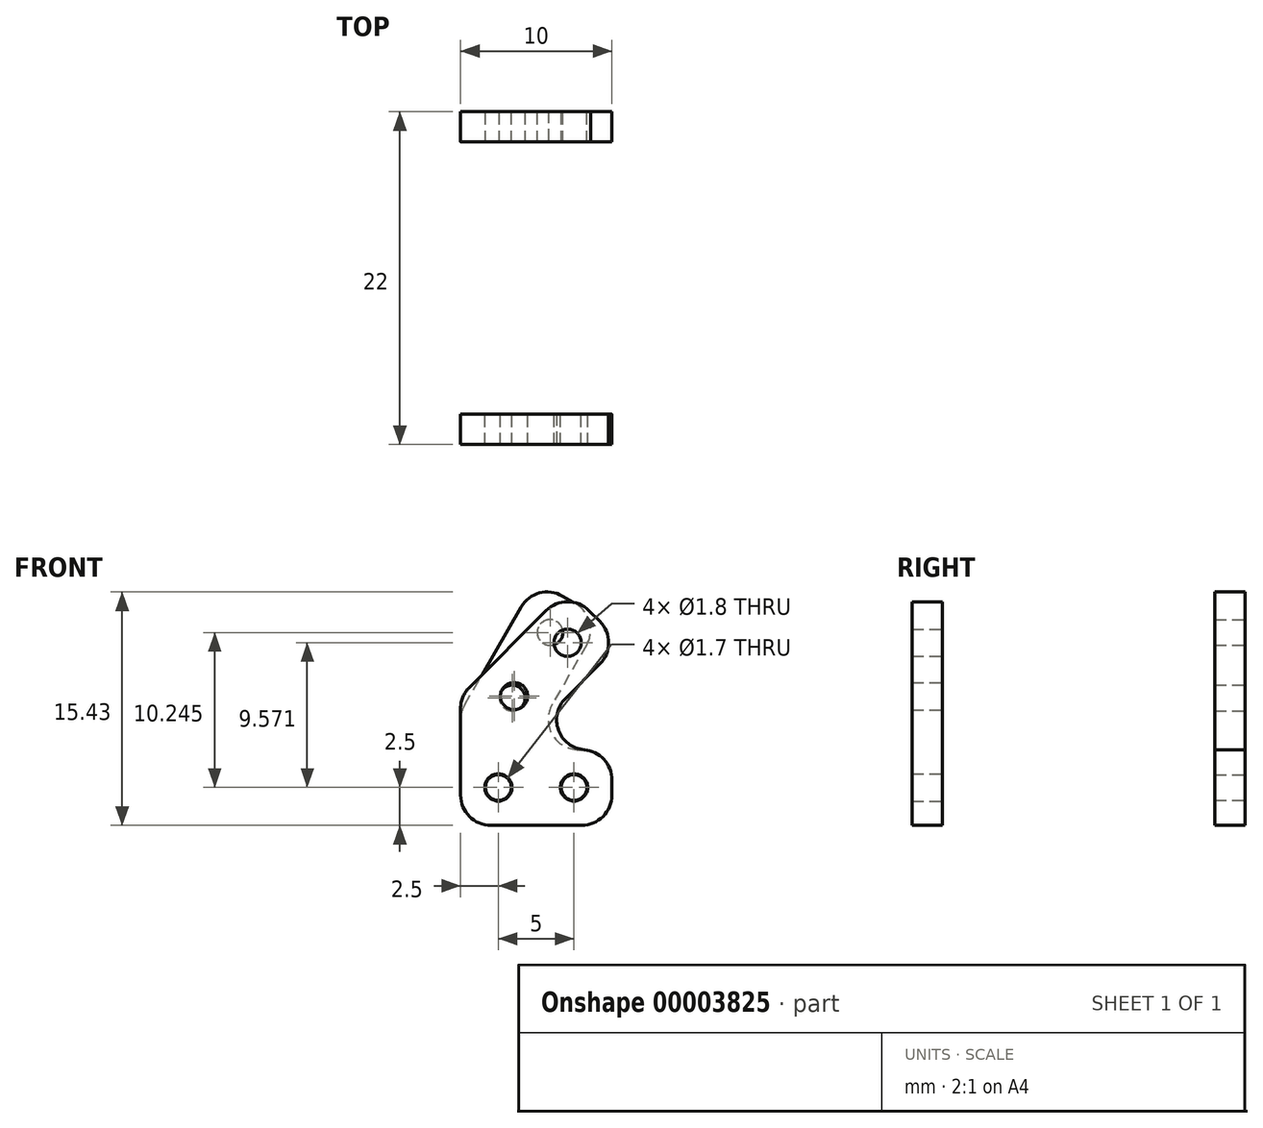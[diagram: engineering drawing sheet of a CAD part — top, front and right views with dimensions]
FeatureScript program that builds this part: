
annotation { "Feature Type Name" : "Feature", "Feature Type Description" : "" }
export const myFeature = defineFeature(function(context is Context, id is Id, definition is map)
    precondition{}
    {
        {
            var Q0;
            Q0=qCreatedBy(makeId("Front.planeOp"),FACE);
            var sketch = newSketch(context, id + "F0", { "sketchPlane" : qUnion([Q0])});
            skLineSegment(sketch, "E0", {"start": v(0, 0) * mm, "end": v(0, 7.5) * mm});
            skLineSegment(sketch, "E1", {"start": v(0, 7.5) * mm, "end": v(5, 16.16) * mm});
            skLineSegment(sketch, "E2", {"start": v(5, 16.16) * mm, "end": v(9.33, 13.66) * mm});
            skLineSegment(sketch, "E3", {"start": v(9.33, 13.66) * mm, "end": v(4.33, 5) * mm});
            skLineSegment(sketch, "E4", {"start": v(4.33, 5) * mm, "end": v(10, 5) * mm});
            skLineSegment(sketch, "E5", {"start": v(10, 5) * mm, "end": v(10, 0) * mm});
            skLineSegment(sketch, "E6", {"start": v(10, 0) * mm, "end": v(0, 0) * mm});
            skLineSegment(sketch, "E7", {"start": v(7.17, 14.91) * mm, "end": v(2.15, 6.22) * mm, "construction": true});
            skCircle(sketch, "E8", {"center": v(5.92, 12.75) * mm, "radius": 0.85 * mm});
            skCircle(sketch, "E9", {"center": v(3.42, 8.42) * mm, "radius": 0.85 * mm});
            skLineSegment(sketch, "E10", {"start": v(10, 2.5) * mm, "end": v(0, 2.5) * mm, "construction": true});
            skCircle(sketch, "E11", {"center": v(2.5, 2.5) * mm, "radius": 0.85 * mm});
            skCircle(sketch, "E12", {"center": v(7.5, 2.5) * mm, "radius": 0.85 * mm});
            skPoint(sketch, "E13.visualSharp", {"position": v(0, 0) * mm});
            skPoint(sketch, "E14.visualSharp", {"position": v(10, 0) * mm});
            skPoint(sketch, "E15.visualSharp", {"position": v(10, 5) * mm});
            skPoint(sketch, "E16.visualSharp", {"position": v(4.33, 5) * mm});
            skPoint(sketch, "E17.visualSharp", {"position": v(9.33, 13.66) * mm});
            skPoint(sketch, "E18.visualSharp", {"position": v(5, 16.16) * mm});
            skPoint(sketch, "E19.visualSharp", {"position": v(0, 7.5) * mm});
            skSolve(sketch);
        }
        {
            var Q0;
            Q0=makeQuery(id+"F0.imprint","IMPRINT",FACE,{"disambiguationData":[TD([[makeQuery(id+"F0.imprint","IMPRINT",EDGE,{"derivedFrom":sQuery(id+"F0.wireOp",EDGE,"E0")}),-1.0]])]});
            extrude(context, id + "F1", {"entities" : qUnion([Q0]), "depth" : 2 * mm});
        }
        {
            var Q0;
            Q0=qCreatedBy(makeId("Front.planeOp"),FACE);
            cPlane(context, id + "F2", {"entities" : qUnion([Q0]), "cplaneType" : CPlaneType.OFFSET, "offset" : 20 * mm, "width" : 150 * mm, "height" : 150 * mm});
        }
        {
            var Q0;
            Q0=qCreatedBy(id+"F2.planeOp",FACE);
            var sketch = newSketch(context, id + "F3", { "sketchPlane" : qUnion([Q0])});
            skLineSegment(sketch, "E20.bottom", {"start": v(0, 0) * mm, "end": v(10, 0) * mm});
            skLineSegment(sketch, "E20.left", {"start": v(0, 0) * mm, "end": v(0, 8.54) * mm});
            skLineSegment(sketch, "E20.right", {"start": v(10, 0) * mm, "end": v(10, 5) * mm});
            skLineSegment(sketch, "E21", {"start": v(0, 8.54) * mm, "end": v(7.07, 15.6) * mm});
            skLineSegment(sketch, "E22", {"start": v(7.07, 15.6) * mm, "end": v(10.6, 12.07) * mm});
            skLineSegment(sketch, "E23", {"start": v(10.6, 12.07) * mm, "end": v(3.54, 5) * mm});
            skLineSegment(sketch, "E24", {"start": v(3.54, 5) * mm, "end": v(10, 5) * mm});
            skLineSegment(sketch, "E25", {"start": v(10, 2.5) * mm, "end": v(0, 2.5) * mm, "construction": true});
            skLineSegment(sketch, "E26", {"start": v(8.84, 13.84) * mm, "end": v(1.86, 6.86) * mm, "construction": true});
            skCircle(sketch, "E27", {"center": v(7.5, 2.5) * mm, "radius": 0.9 * mm});
            skCircle(sketch, "E28", {"center": v(2.5, 2.5) * mm, "radius": 0.9 * mm});
            skCircle(sketch, "E29", {"center": v(7.07, 12.07) * mm, "radius": 0.9 * mm});
            skCircle(sketch, "E30", {"center": v(3.54, 8.54) * mm, "radius": 0.9 * mm});
            skSolve(sketch);
        }
        {
            var Q0;
            Q0=makeQuery(id+"F3.imprint","IMPRINT",FACE,{"disambiguationData":[TD([[makeQuery(id+"F3.imprint","IMPRINT",EDGE,{"derivedFrom":sQuery(id+"F3.wireOp",EDGE,"E20.bottom")}),1.0]])]});
            extrude(context, id + "F4", {"entities" : qUnion([Q0]), "depth" : 2 * mm});
        }
        {
            var Q0;
            Q0=makeQuery(id+"F4.opExtrude","SWEPT_EDGE",EDGE,{"disambiguationData":[OSD([sQuery(id+"F3.wireOp",EDGE,"E20.right"),sQuery(id+"F3.wireOp",EDGE,"E24")])]});
            var Q1;
            Q1=makeQuery(id+"F4.opExtrude","SWEPT_EDGE",EDGE,{"disambiguationData":[OSD([sQuery(id+"F3.wireOp",EDGE,"E20.bottom"),sQuery(id+"F3.wireOp",EDGE,"E20.left")])]});
            var Q2;
            Q2=makeQuery(id+"F4.opExtrude","SWEPT_EDGE",EDGE,{"disambiguationData":[OSD([sQuery(id+"F3.wireOp",EDGE,"E20.left"),sQuery(id+"F3.wireOp",EDGE,"E21")])]});
            var Q3;
            Q3=makeQuery(id+"F4.opExtrude","SWEPT_EDGE",EDGE,{"disambiguationData":[OSD([sQuery(id+"F3.wireOp",EDGE,"E20.bottom"),sQuery(id+"F3.wireOp",EDGE,"E20.right")])]});
            var Q4;
            Q4=makeQuery(id+"F4.opExtrude","SWEPT_EDGE",EDGE,{"disambiguationData":[OSD([sQuery(id+"F3.wireOp",EDGE,"E21"),sQuery(id+"F3.wireOp",EDGE,"E22")])]});
            var Q5;
            Q5=makeQuery(id+"F4.opExtrude","SWEPT_EDGE",EDGE,{"disambiguationData":[OSD([sQuery(id+"F3.wireOp",EDGE,"E22"),sQuery(id+"F3.wireOp",EDGE,"E23")])]});
            fillet(context, id + "F5", {"entities" : qUnion([Q0, Q1, Q2, Q3, Q4, Q5]), "radius" : 2 * mm, "tangentPropagation" : true, "allowEdgeOverflow" : false});
        }
        {
            var Q0;
            Q0=makeQuery(id+"F4.opExtrude","SWEPT_EDGE",EDGE,{"disambiguationData":[OSD([sQuery(id+"F3.wireOp",EDGE,"E23"),sQuery(id+"F3.wireOp",EDGE,"E24")])]});
            fillet(context, id + "F6", {"entities" : qUnion([Q0]), "radius" : 2 * mm, "tangentPropagation" : true, "allowEdgeOverflow" : false});
        }
        {
            var Q0;
            Q0=makeQuery(id+"F1.opExtrude","SWEPT_EDGE",EDGE,{"disambiguationData":[OSD([sQuery(id+"F0.wireOp",EDGE,"E4"),sQuery(id+"F0.wireOp",EDGE,"E5")])]});
            var Q1;
            Q1=makeQuery(id+"F1.opExtrude","SWEPT_EDGE",EDGE,{"disambiguationData":[OSD([sQuery(id+"F0.wireOp",EDGE,"E5"),sQuery(id+"F0.wireOp",EDGE,"E6")])]});
            var Q2;
            Q2=makeQuery(id+"F1.opExtrude","SWEPT_EDGE",EDGE,{"disambiguationData":[OSD([sQuery(id+"F0.wireOp",EDGE,"E1"),sQuery(id+"F0.wireOp",EDGE,"E2")])]});
            var Q3;
            Q3=makeQuery(id+"F1.opExtrude","SWEPT_EDGE",EDGE,{"disambiguationData":[OSD([sQuery(id+"F0.wireOp",EDGE,"E0"),sQuery(id+"F0.wireOp",EDGE,"E1")])]});
            var Q4;
            Q4=makeQuery(id+"F1.opExtrude","SWEPT_EDGE",EDGE,{"disambiguationData":[OSD([sQuery(id+"F0.wireOp",EDGE,"E0"),sQuery(id+"F0.wireOp",EDGE,"E6")])]});
            var Q5;
            Q5=makeQuery(id+"F1.opExtrude","SWEPT_EDGE",EDGE,{"disambiguationData":[OSD([sQuery(id+"F0.wireOp",EDGE,"E2"),sQuery(id+"F0.wireOp",EDGE,"E3")])]});
            fillet(context, id + "F7", {"entities" : qUnion([Q0, Q1, Q2, Q3, Q4, Q5]), "radius" : 2 * mm, "tangentPropagation" : true, "allowEdgeOverflow" : false});
        }
        {
            var Q0;
            Q0=makeQuery(id+"F1.opExtrude","SWEPT_EDGE",EDGE,{"disambiguationData":[OSD([sQuery(id+"F0.wireOp",EDGE,"E3"),sQuery(id+"F0.wireOp",EDGE,"E4")])]});
            fillet(context, id + "F8", {"entities" : qUnion([Q0]), "radius" : 2 * mm, "tangentPropagation" : true, "allowEdgeOverflow" : false});
        }
    });
